# Revit family: NBS_ConceptCubicleSystems_PnlCbclSym_FastTrack
name_source: partatom
category: Specialty Equipment
units: mm (PartAtom-declared; Revit-internal decimal feet)

## family parameters
Always vertical = Yes
Cut with Voids When Loaded = No
Part Type = Normal
Room Calculation Point = No
Round Connector Dimension = Use Diameter
Shared = No
Work Plane-Based = No

## types (8) — shared parameters
AssetType = Fixed
Category = Ss_25_12_60_60:Panel cubicle systems
Color = White, light grey, cream, oak, red, yellow, blue or a mixture of two
Description = Fast track cubicles, ideal for low use dry areas
DoorLeafMaterial = NBS_ConceptCubicleSystems_V110_VertImperial-Green
DurationUnit = year
FittingMaterial = NBS_ConceptCubicleSystems_SatinAnodisedAluminium
Fittings = Satin anodised aluminium
IfcExportAs = IfcFurnitureType
IfcExportType = USERDEFINED
IsBuiltIn = Yes
ManufacturerName = Concept Cubicle Systems
ManufacturerURL = www.conceptcubiclesystems.co.uk
Material = Melamine Faced Chipboard
ModelReference = Fast Track Cubicles
NBSCertification = www.nationalbimlibrary.com/cert/aduvk2um
NBSDescription = Panel cubicle system
NBSReference = 25-05-60/160
PanelSupports = 150 mm
PanelThickness = 18 mm  [stored 0.0590551 ft]
Panels = 18 mm melamine faced chipboard
PartitionMaterial = NBS_ConceptCubicleSystems_V110_VertImperial-Green
PilasterMaterial = NBS_ConceptCubicleSystems_V110_VertImperial-Green
ProductInformation = https://www.conceptcubiclesystems.co.uk
Size = 1500 x 1950 mm
Status = UNSET
Style = Cubicle
SystemManufacturer = Concept Cubicle Systems
Uniclass2015Code = Ss_25_12_60_60
Uniclass2015Title = Panel cubicle systems
Uniclass2015Version = Systems v1.17
Version = 3
WarrantyDurationUnit = year

## per-type parameters (varying)
| type | BIMObjectName | HasFittingsLeft | HasFittingsRight | HasPartitionLeft | HasPartitionRight | HasPilasterPanelReturnLeft | HasPilasterPanelReturnRight | IsEndCubicle | IsFirstCubicle | IsMiddleCubicle | IsSingleCubicle | IsWallEndEndCubicle | IsWallEndFirstCubicle | IsWallEndSingleCubicle | IsWallToWallSingleCubicle | Name | PilasterPanelReturnLeft | PilasterPanelReturnRight |
| SingleCubicle | NBS_ConceptCubicleSystems_PanelCubicleSystem_FastTrack_SingleCubicle | No | No | Yes | Yes | Yes | Yes | No | No | No | Yes | No | No | No | No | PanelCubicleSystem_FastTrack_SingleCubicle_ConceptCubicleSystems | 9 mm  [stored 0.0295276 ft] | 9 mm  [stored 0.0295276 ft] |
| WallToWallSingleCubicle | NBS_ConceptCubicleSystems_PanelCubicleSystem_FastTrack_WallToWallSingleCubicle | Yes | Yes | No | No | No | No | No | No | No | No | No | No | No | Yes | PanelCubicleSystem_FastTrack_WallToWallSingleCubicle_ConceptCubicleSystems | 0 mm  [stored 0 ft] | 0 mm  [stored 0 ft] |
| EndCubicle | NBS_ConceptCubicleSystems_PanelCubicleSystem_FastTrack_EndCubicle | No | No | No | Yes | No | Yes | Yes | No | No | No | No | No | No | No | PanelCubicleSystem_FastTrack_EndCubicle_ConceptCubicleSystems | 0 mm  [stored 0 ft] | 9 mm  [stored 0.0295276 ft] |
| FirstCubicle | NBS_ConceptCubicleSystems_PanelCubicleSystem_FastTrack_FirstCubicle | No | No | Yes | Yes | Yes | No | No | Yes | No | No | No | No | No | No | PanelCubicleSystem_FastTrack_FirstCubicle_ConceptCubicleSystems | 9 mm  [stored 0.0295276 ft] | 0 mm  [stored 0 ft] |
| WallEndFirstCubicle | NBS_ConceptCubicleSystems_PanelCubicleSystem_FastTrack_WallEndFirstCubicle | Yes | No | No | Yes | No | No | No | No | No | No | No | Yes | No | No | PanelCubicleSystem_FastTrack_WallEndFirstCubicle_ConceptCubicleSystems | 0 mm  [stored 0 ft] | 0 mm  [stored 0 ft] |
| WallEndSingleCubicle | NBS_ConceptCubicleSystems_PanelCubicleSystem_FastTrack_WallEndSingleCubicle | Yes | No | No | Yes | No | Yes | No | No | No | No | No | No | Yes | No | PanelCubicleSystem_FastTrack_WallEndSingleCubicle_ConceptCubicleSystems | 0 mm  [stored 0 ft] | 9 mm  [stored 0.0295276 ft] |
| MiddleCubicle | NBS_ConceptCubicleSystems_PanelCubicleSystem_FastTrack_MiddleCubicle | No | No | No | Yes | No | No | No | No | Yes | No | No | No | No | No | PanelCubicleSystem_FastTrack_MiddleCubicle_ConceptCubicleSystems | 0 mm  [stored 0 ft] | 0 mm  [stored 0 ft] |
| WallEndEndCubicle | NBS_ConceptCubicleSystems_PanelCubicleSystem_FastTrack_WallEndEndCubicle | No | Yes | No | No | No | No | No | No | No | No | Yes | No | No | No | PanelCubicleSystem_FastTrack_WallEndEndCubicle_ConceptCubicleSystems | 0 mm  [stored 0 ft] | 0 mm  [stored 0 ft] |

note: [stored X ft] marks values corroborated as IEEE doubles in the binary element streams (Revit-internal decimal feet)

## geometry (parser evidence)
native form markers: Sweep x5
no freeform markers — native parametric forms only
